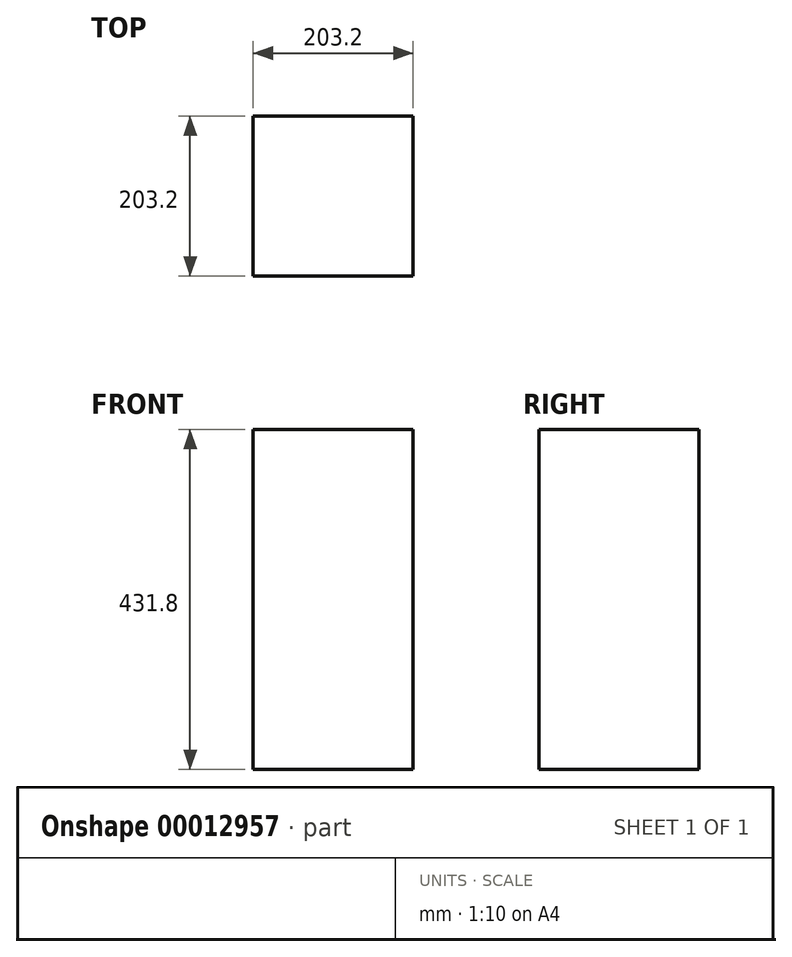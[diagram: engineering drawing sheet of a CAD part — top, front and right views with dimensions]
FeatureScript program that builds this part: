
annotation { "Feature Type Name" : "Feature", "Feature Type Description" : "" }
export const myFeature = defineFeature(function(context is Context, id is Id, definition is map)
    precondition{}
    {
        {
            var Q0;
            Q0=qCreatedBy(makeId("Top.planeOp"),FACE);
            var sketch = newSketch(context, id + "F0", { "sketchPlane" : qUnion([Q0])});
            skLineSegment(sketch, "E0.rect.bottom", {"start": v(101.6, -101.6) * mm, "end": v(-101.6, -101.6) * mm});
            skLineSegment(sketch, "E0.rect.top", {"start": v(101.6, 101.6) * mm, "end": v(-101.6, 101.6) * mm});
            skLineSegment(sketch, "E0.rect.left", {"start": v(101.6, -101.6) * mm, "end": v(101.6, 101.6) * mm});
            skLineSegment(sketch, "E0.rect.right", {"start": v(-101.6, -101.6) * mm, "end": v(-101.6, 101.6) * mm});
            skPoint(sketch, "E0.rect.middle", {"position": v(0, 0) * mm});
            skSolve(sketch);
        }
        {
            var Q0;
            Q0=makeQuery(id+"F0.imprint","IMPRINT",FACE,{"disambiguationData":[TD([[makeQuery(id+"F0.imprint","IMPRINT",EDGE,{"derivedFrom":sQuery(id+"F0.wireOp",EDGE,"E0.rect.bottom")}),-1.0]])]});
            extrude(context, id + "F1", {"entities" : qUnion([Q0]), "depth" : 431.8 * mm});
        }
    });
